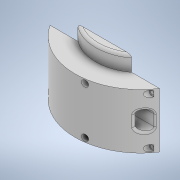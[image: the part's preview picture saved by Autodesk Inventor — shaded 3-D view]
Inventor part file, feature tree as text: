
AUTODESK INVENTOR PART (.ipt)
format: ipt  version: 2021 (Build 250183000, 183)  size: 580,096 bytes
history: native  units: mm
features: extrude x12, sketch x12, fillet x3, other x1
ambient origin geometry x8: Origin, YZ Plane, XZ Plane, XY Plane, X Axis, Y Axis, Z Axis, Center Point
bodies: Body1 (feature_tree)
feature tree (28):
  other  "Bryła1"
  extrude  "Wyciągnięcie proste1"  Depth=53.0mm TaperAngle=0.0deg
  extrude  "Wyciągnięcie proste2"  Depth=65.0mm
  extrude  "Wyciągnięcie proste3"  Depth=2.0mm TaperAngle=0.0deg
  extrude  "Wyciągnięcie proste5"  Depth=65.0mm
  extrude  "Wyciągnięcie proste7"  Depth=11.0mm TaperAngle=0.0deg
  extrude  "Wyciągnięcie proste8"  Depth=4.0mm TaperAngle=0.0deg
  extrude  "Wyciągnięcie proste9"  Depth=4.0mm
  fillet  "Zaokrąglenie2"  Radius=4.0mm
  fillet  "Zaokrąglenie3"  [1 undecoded]
  extrude  "Wyciągnięcie proste14"  Depth=4.0mm TaperAngle=0.0deg
  fillet  "Zaokrąglenie5"  Radius=25.805mm
  extrude  "Wyciągnięcie proste15"  Depth=3.0mm
  extrude  "Wyciągnięcie proste16"  Depth=1.5mm
  extrude  "Wyciągnięcie proste17"  Depth=1.0mm TaperAngle=0.0deg
  extrude  "Wyciągnięcie proste18"  Depth=2.0mm
  sketch  "Szkic1"
  sketch  "Szkic3"
  sketch  "Szkic4"
  sketch  "Szkic5"
  sketch  "Szkic11"
  sketch  "Szkic13"
  sketch  "Szkic14"
  sketch  "Szkic21"
  sketch  "Szkic22"
  sketch  "Szkic23"
  sketch  "Szkic26"
  sketch  "Szkic27"
note: 1 required parameter value undecoded (feature->parameter linkage not recoverable at this tier; creation-order binding heuristic only, values carry confidence <= 0.55)
